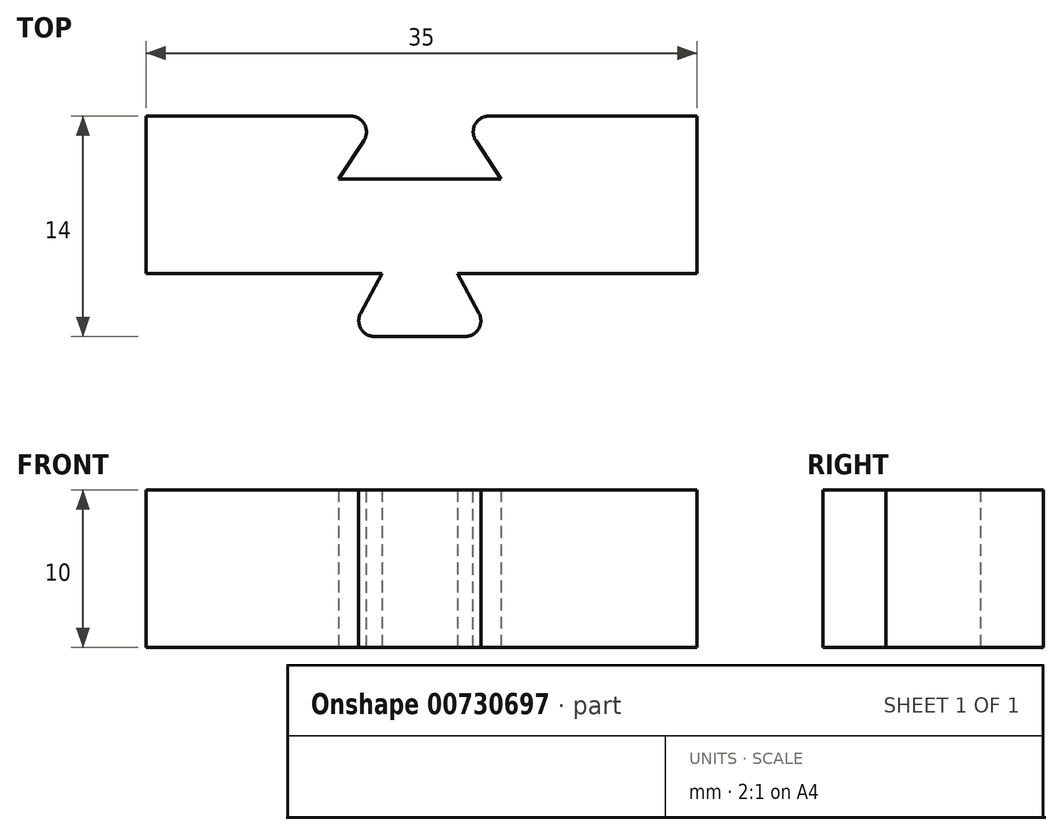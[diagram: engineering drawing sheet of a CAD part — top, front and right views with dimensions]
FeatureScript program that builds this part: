
annotation { "Feature Type Name" : "Feature", "Feature Type Description" : "" }
export const myFeature = defineFeature(function(context is Context, id is Id, definition is map)
    precondition{}
    {
        {
            var Q0;
            Q0=qCreatedBy(makeId("Top.planeOp"),FACE);
            var sketch = newSketch(context, id + "F0", { "sketchPlane" : qUnion([Q0])});
            skLineSegment(sketch, "E0.bottom", {"start": v(17.5, -5) * mm, "end": v(-17.5, -5) * mm});
            skLineSegment(sketch, "E0.top", {"start": v(17.5, 5) * mm, "end": v(-17.5, 5) * mm});
            skLineSegment(sketch, "E0.left", {"start": v(17.5, -5) * mm, "end": v(17.5, 5) * mm});
            skLineSegment(sketch, "E0.right", {"start": v(-17.5, -5) * mm, "end": v(-17.5, 5) * mm});
            skPoint(sketch, "E0.middle", {"position": v(0, 0) * mm});
            skLineSegment(sketch, "E1", {"start": v(-17.5, -5) * mm, "end": v(-2.5, -5) * mm, "construction": true});
            skLineSegment(sketch, "E2", {"start": v(-17.5, 5) * mm, "end": v(-2.65, 5) * mm, "construction": true});
            skLineSegment(sketch, "E3", {"start": v(-2.5, -5) * mm, "end": v(2.3, -5) * mm, "construction": true});
            skLineSegment(sketch, "E4", {"start": v(-2.5, -5) * mm, "end": v(-4.65, -9) * mm});
            skLineSegment(sketch, "E5", {"start": v(-4.65, -9) * mm, "end": v(4.45, -9) * mm});
            skLineSegment(sketch, "E6", {"start": v(4.45, -9) * mm, "end": v(2.3, -5) * mm});
            skLineSegment(sketch, "E7", {"start": v(-0.1, -9) * mm, "end": v(-0.1, -5) * mm, "construction": true});
            skLineSegment(sketch, "E8", {"start": v(-2.65, 5) * mm, "end": v(2.45, 5) * mm, "construction": true});
            skLineSegment(sketch, "E9", {"start": v(-2.65, 5) * mm, "end": v(-5.25, 1) * mm});
            skLineSegment(sketch, "E10", {"start": v(-5.25, 1) * mm, "end": v(5.05, 1) * mm});
            skLineSegment(sketch, "E11", {"start": v(5.05, 1) * mm, "end": v(2.45, 5) * mm});
            skPoint(sketch, "E12.endSnap0", {"position": v(-0.1, 1) * mm});
            skLineSegment(sketch, "E13", {"start": v(-0.1, 1) * mm, "end": v(-0.1, 5) * mm, "construction": true});
            skSolve(sketch);
        }
        {
            var Q0;
            {var subQ0=sQuery(id+"F0.wireOp",EDGE,"E0.left");Q0=makeQuery(id+"F0.imprint","IMPRINT",FACE,{"disambiguationData":[TD([[makeQuery(id+"F0.imprint","IMPRINT",EDGE,{"derivedFrom":subQ0}),1.0]])]});}
            var Q1;
            {var subQ0=sQuery(id+"F0.wireOp",EDGE,"E4");Q1=makeQuery(id+"F0.imprint","IMPRINT",FACE,{"disambiguationData":[TD([[makeQuery(id+"F0.imprint","IMPRINT",EDGE,{"derivedFrom":subQ0}),1.0]])]});}
            var Q2;
            {var subQ0=sQuery(id+"F0.wireOp",EDGE,"mANhPHhZ-PdHe-0qNs-CDWU-keSWBgpjLTlN");Q2=makeQuery(id+"F0.imprint","IMPRINT",FACE,{"disambiguationData":[TD([[makeQuery(id+"F0.imprint","IMPRINT",EDGE,{"derivedFrom":subQ0}),-1.0]])]});}
            extrude(context, id + "F1", {"entities" : qUnion([Q0, Q1, Q2]), "depth" : 10 * mm, "offsetDistance" : 25 * mm});
        }
        {
            var Q0;
            Q0=makeQuery(id+"F1.opExtrude","SWEPT_EDGE",EDGE,{"disambiguationData":[OSD([sQuery(id+"F0.wireOp",EDGE,"E0.top"),sQuery(id+"F0.wireOp",EDGE,"E9")])]});
            var Q1;
            Q1=makeQuery(id+"F1.opExtrude","SWEPT_EDGE",EDGE,{"disambiguationData":[OSD([sQuery(id+"F0.wireOp",EDGE,"E0.top"),sQuery(id+"F0.wireOp",EDGE,"E11")])]});
            var Q2;
            Q2=makeQuery(id+"F1.opExtrude","SWEPT_EDGE",EDGE,{"disambiguationData":[OSD([sQuery(id+"F0.wireOp",EDGE,"E5"),sQuery(id+"F0.wireOp",EDGE,"E6")])]});
            var Q3;
            Q3=makeQuery(id+"F1.opExtrude","SWEPT_EDGE",EDGE,{"disambiguationData":[OSD([sQuery(id+"F0.wireOp",EDGE,"E4"),sQuery(id+"F0.wireOp",EDGE,"E5")])]});
            fillet(context, id + "F2", {"entities" : qUnion([Q0, Q1, Q2, Q3]), "radius" : 1 * mm, "tangentPropagation" : true, "allowEdgeOverflow" : false});
        }
    });
